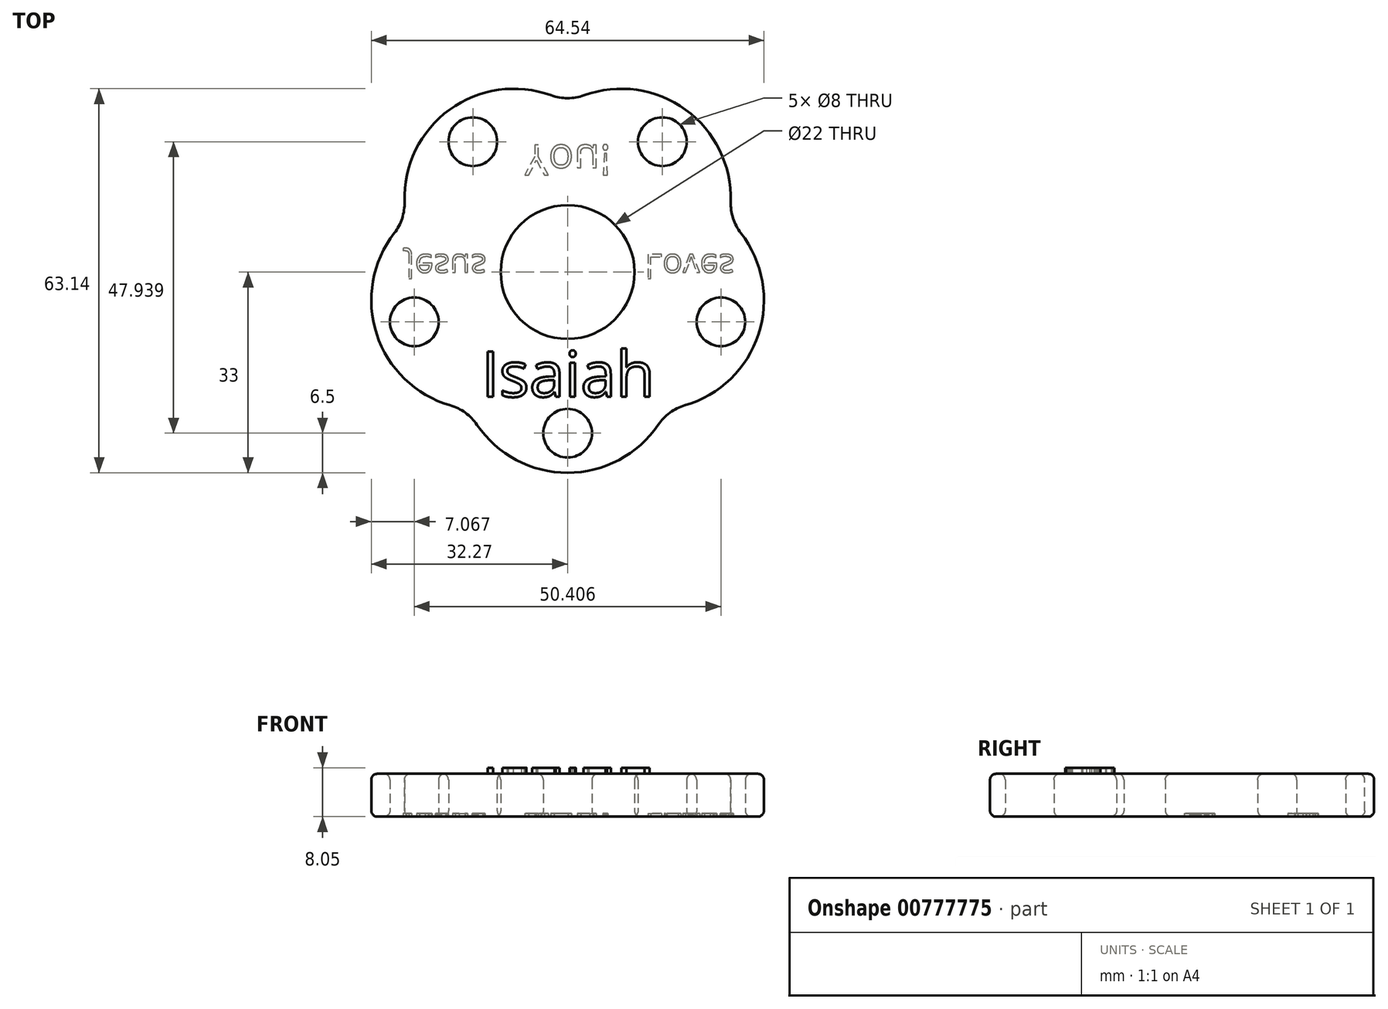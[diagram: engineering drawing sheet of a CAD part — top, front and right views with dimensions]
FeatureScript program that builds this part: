
annotation { "Feature Type Name" : "Feature", "Feature Type Description" : "" }
export const myFeature = defineFeature(function(context is Context, id is Id, definition is map)
    precondition{}
    {
        {
            var Q0;
            Q0=qCreatedBy(makeId("Top.planeOp"),FACE);
            var sketch = newSketch(context, id + "F0", { "sketchPlane" : qUnion([Q0])});
            skCircle(sketch, "E0.cCircle", {"center": v(0, 0) * mm, "radius": 15 * mm, "construction": true});
            skPoint(sketch, "E0.0.midPoint", {"position": v(8.82, 12.14) * mm});
            skArc(sketch, "E1", {"start": v(0, 27.83) * mm, "mid": v(-19.4, 26.7) * mm, "end": v(-26.47, 8.6) * mm});
            skArc(sketch, "E2", {"start": v(26.47, 8.6) * mm, "mid": v(19.4, 26.7) * mm, "end": v(0, 27.83) * mm});
            skArc(sketch, "E3", {"start": v(16.36, -22.51) * mm, "mid": v(31.38, -10.2) * mm, "end": v(26.47, 8.6) * mm});
            skArc(sketch, "E4", {"start": v(-16.36, -22.51) * mm, "mid": v(0, -33) * mm, "end": v(16.36, -22.51) * mm});
            skArc(sketch, "E5", {"start": v(-26.47, 8.6) * mm, "mid": v(-31.38, -10.2) * mm, "end": v(-16.36, -22.51) * mm});
            skCircle(sketch, "E6", {"center": v(0, 0) * mm, "radius": 27.83 * mm, "construction": true});
            skCircle(sketch, "E7", {"center": v(0, 0) * mm, "radius": 11 * mm});
            skCircle(sketch, "E8", {"center": v(-15.58, 21.44) * mm, "radius": 4 * mm});
            skCircle(sketch, "E9", {"center": v(15.58, 21.44) * mm, "radius": 4 * mm});
            skCircle(sketch, "E10", {"center": v(25.2, -8.19) * mm, "radius": 4 * mm});
            skCircle(sketch, "E11", {"center": v(0, -26.5) * mm, "radius": 4 * mm});
            skCircle(sketch, "E12", {"center": v(-25.2, -8.19) * mm, "radius": 4 * mm});
            skCircle(sketch, "E13", {"center": v(0, 0) * mm, "radius": 26.5 * mm, "construction": true});
            skLineSegment(sketch, "E14", {"start": v(0, 0) * mm, "end": v(0, 61.86) * mm, "construction": true});
            skLineSegment(sketch, "E15", {"start": v(0, 0) * mm, "end": v(32.6, 44.86) * mm, "construction": true});
            skLineSegment(sketch, "E16", {"start": v(0, 0) * mm, "end": v(66.5, -21.6) * mm, "construction": true});
            skLineSegment(sketch, "E17", {"start": v(0, 0) * mm, "end": v(0, -30.5) * mm, "construction": true});
            skLineSegment(sketch, "E18", {"start": v(0, 0) * mm, "end": v(-58.05, -18.86) * mm, "construction": true});
            skLineSegment(sketch, "E19", {"start": v(0, 0) * mm, "end": v(-29.25, 40.26) * mm, "construction": true});
            skSolve(sketch);
        }
        {
            var Q0;
            Q0=qSketchRegion(id+"F0",true);
            extrude(context, id + "F1", {"entities" : qUnion([Q0]), "depth" : 7.05 * mm, "offsetDistance" : 25.4 * mm});
        }
        {
            var Q0;
            Q0=makeQuery(id+"F1.opExtrude","SWEPT_EDGE",EDGE,{"disambiguationData":[OSD([sQuery(id+"F0.wireOp",EDGE,"E3"),sQuery(id+"F0.wireOp",EDGE,"E4")])]});
            var Q1;
            Q1=makeQuery(id+"F1.opExtrude","SWEPT_EDGE",EDGE,{"disambiguationData":[OSD([sQuery(id+"F0.wireOp",EDGE,"E2"),sQuery(id+"F0.wireOp",EDGE,"E3")])]});
            var Q2;
            Q2=makeQuery(id+"F1.opExtrude","SWEPT_EDGE",EDGE,{"disambiguationData":[OSD([sQuery(id+"F0.wireOp",EDGE,"E1"),sQuery(id+"F0.wireOp",EDGE,"E2")])]});
            var Q3;
            Q3=makeQuery(id+"F1.opExtrude","SWEPT_EDGE",EDGE,{"disambiguationData":[OSD([sQuery(id+"F0.wireOp",EDGE,"E1"),sQuery(id+"F0.wireOp",EDGE,"E5")])]});
            var Q4;
            Q4=makeQuery(id+"F1.opExtrude","SWEPT_EDGE",EDGE,{"disambiguationData":[OSD([sQuery(id+"F0.wireOp",EDGE,"E4"),sQuery(id+"F0.wireOp",EDGE,"E5")])]});
            fillet(context, id + "F2", {"entities" : qUnion([Q0, Q1, Q2, Q3, Q4]), "radius" : 8 * mm, "tangentPropagation" : true, "allowEdgeOverflow" : false});
        }
        {
            var Q0;
            Q0=makeQuery(id+"F1.opExtrude","CAP_FACE",FACE,{"disambiguationData":[OSD([sQuery(id+"F0.wireOp",EDGE,"E1"),sQuery(id+"F0.wireOp",EDGE,"E2"),sQuery(id+"F0.wireOp",EDGE,"E3"),sQuery(id+"F0.wireOp",EDGE,"E4"),sQuery(id+"F0.wireOp",EDGE,"E5"),sQuery(id+"F0.wireOp",EDGE,"E7"),sQuery(id+"F0.wireOp",EDGE,"E8"),sQuery(id+"F0.wireOp",EDGE,"E9"),sQuery(id+"F0.wireOp",EDGE,"E10"),sQuery(id+"F0.wireOp",EDGE,"E11"),sQuery(id+"F0.wireOp",EDGE,"E12")])],"isStart":false});
            var Q1;
            Q1=makeQuery(id+"F1.opExtrude","CAP_FACE",FACE,{"disambiguationData":[OSD([sQuery(id+"F0.wireOp",EDGE,"E1"),sQuery(id+"F0.wireOp",EDGE,"E2"),sQuery(id+"F0.wireOp",EDGE,"E3"),sQuery(id+"F0.wireOp",EDGE,"E4"),sQuery(id+"F0.wireOp",EDGE,"E5"),sQuery(id+"F0.wireOp",EDGE,"E7"),sQuery(id+"F0.wireOp",EDGE,"E8"),sQuery(id+"F0.wireOp",EDGE,"E9"),sQuery(id+"F0.wireOp",EDGE,"E10"),sQuery(id+"F0.wireOp",EDGE,"E11"),sQuery(id+"F0.wireOp",EDGE,"E12")])],"isStart":true});
            fillet(context, id + "F3", {"entities" : qUnion([Q0, Q1]), "radius" : 1 * mm, "tangentPropagation" : true, "allowEdgeOverflow" : false});
        }
        {
            var Q0;
            Q0=makeQuery(id+"F1.opExtrude","CAP_FACE",FACE,{"disambiguationData":[OSD([sQuery(id+"F0.wireOp",EDGE,"E1"),sQuery(id+"F0.wireOp",EDGE,"E2"),sQuery(id+"F0.wireOp",EDGE,"E3"),sQuery(id+"F0.wireOp",EDGE,"E4"),sQuery(id+"F0.wireOp",EDGE,"E5"),sQuery(id+"F0.wireOp",EDGE,"E7"),sQuery(id+"F0.wireOp",EDGE,"E8"),sQuery(id+"F0.wireOp",EDGE,"E9"),sQuery(id+"F0.wireOp",EDGE,"E10"),sQuery(id+"F0.wireOp",EDGE,"E11"),sQuery(id+"F0.wireOp",EDGE,"E12")])],"isStart":false});
            var sketch = newSketch(context, id + "F4", { "sketchPlane" : qUnion([Q0])});
            skText(sketch, "E20", { "text": "Isaiah", "fontName": "OpenSans-Regular.ttf"});
            const initialGuessF4  = {"E20": [-0.01416, -0.0205, 1, 0, 0.0075]};
            skSetInitialGuess(sketch, initialGuessF4);
            skSolve(sketch);
        }
        {
            var Q0;
            Q0=qSketchRegion(id+"F4",true);
            extrude(context, id + "F5", {"entities" : qUnion([Q0]), "operationType" : NewBodyOperationType.ADD, "depth" : 1 * mm, "offsetDistance" : 25 * mm});
        }
        {
            var Q0;
            Q0=makeQuery(id+"F1.opExtrude","CAP_FACE",FACE,{"disambiguationData":[OSD([sQuery(id+"F0.wireOp",EDGE,"E1"),sQuery(id+"F0.wireOp",EDGE,"E2"),sQuery(id+"F0.wireOp",EDGE,"E3"),sQuery(id+"F0.wireOp",EDGE,"E4"),sQuery(id+"F0.wireOp",EDGE,"E5"),sQuery(id+"F0.wireOp",EDGE,"E7"),sQuery(id+"F0.wireOp",EDGE,"E8"),sQuery(id+"F0.wireOp",EDGE,"E9"),sQuery(id+"F0.wireOp",EDGE,"E10"),sQuery(id+"F0.wireOp",EDGE,"E11"),sQuery(id+"F0.wireOp",EDGE,"E12")])],"isStart":true});
            var sketch = newSketch(context, id + "F6", { "sketchPlane" : qUnion([Q0])});
            skText(sketch, "E21", { "text": "Jesus                  Loves", "fontName": "OpenSans-Regular.ttf"});
            skText(sketch, "E22", { "text": "You!", "fontName": "OpenSans-Regular.ttf"});
            const initialGuessF6  = {"E21": [-0.02661, -0.0029, 1, 0, 0.004], "E22": [-0.00706, -0.02088, 1, 0, 0.005]};
            skSetInitialGuess(sketch, initialGuessF6);
            skSolve(sketch);
        }
        {
            var Q0;
            Q0=qSketchRegion(id+"F6",true);
            extrude(context, id + "F7", {"entities" : qUnion([Q0]), "operationType" : NewBodyOperationType.REMOVE, "oppositeDirection" : true, "depth" : .5 * mm, "offsetDistance" : 25 * mm});
        }
    });
